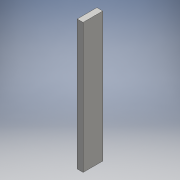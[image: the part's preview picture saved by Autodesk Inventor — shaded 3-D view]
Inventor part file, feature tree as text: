
AUTODESK INVENTOR PART (.ipt)
format: ipt  version: 2016 (Build 200138000, 138)  size: 88,064 bytes
history: native  units: mm
features: other x1, extrude x1, sketch x1
ambient origin geometry x8: Origin, YZ Plane, XZ Plane, XY Plane, X Axis, Y Axis, Z Axis, Center Point
bodies: Body1 (feature_tree)
feature tree (3):
  other  "Bryła1"
  extrude  "Wyciągnięcie proste1"  Depth=66.0mm
  sketch  "Szkic1"
